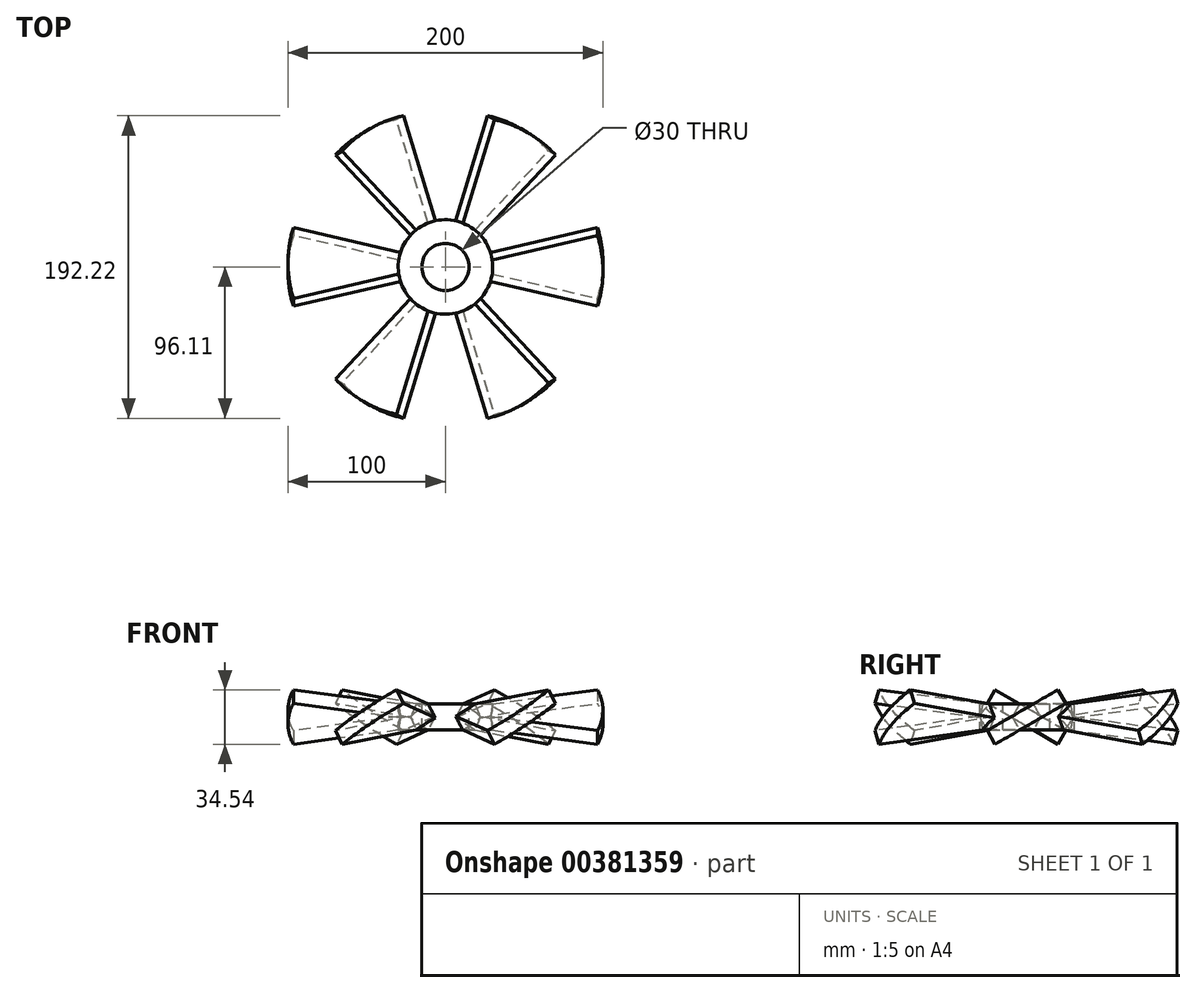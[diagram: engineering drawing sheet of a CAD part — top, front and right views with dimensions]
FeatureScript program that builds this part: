
annotation { "Feature Type Name" : "Feature", "Feature Type Description" : "" }
export const myFeature = defineFeature(function(context is Context, id is Id, definition is map)
    precondition{}
    {
        {
            var Q0;
            Q0=qCreatedBy(makeId("Top.planeOp"),FACE);
            var sketch = newSketch(context, id + "F0", { "sketchPlane" : qUnion([Q0])});
            skArc(sketch, "E0", {"start": v(96.6, 25.88) * mm, "mid": v(100, 0) * mm, "end": v(96.6, -25.88) * mm});
            skLineSegment(sketch, "E1", {"start": v(0, 0) * mm, "end": v(96.6, -25.88) * mm});
            skLineSegment(sketch, "E2.MirrorCS", {"start": v(0, 0) * mm, "end": v(96.6, 25.88) * mm});
            skLineSegment(sketch, "E3", {"start": v(0, 0) * mm, "end": v(116.16, 0) * mm, "construction": true});
            skSolve(sketch);
        }
        {
            var Q0;
            Q0 = qSketchRegion(id + "F0", true);
            extrude(context, id + "F1", {"entities" : qUnion([Q0]), "endBound" : BoundingType.SYMMETRIC, "depth" : 10 * mm});
        }
        {
            var Q0;
            Q0=makeQuery(id+"F1.opExtrude","SWEPT_BODY",BODY,{"disambiguationData":[OSD([sQuery(id+"F0.wireOp",EDGE,"E0"),sQuery(id+"F0.wireOp",EDGE,"E1"),sQuery(id+"F0.wireOp",EDGE,"E2.MirrorCS")])]});
            var Q1;
            Q1=sQuery(id+"F0.wireOp",EDGE,"E3");
            transform(context, id + "F2", {"entities" : qUnion([Q0]), "transformType" : TransformType.ROTATION, "transformAxis" : qUnion([Q1]), "angle" : 30 * degree, "makeCopy" : false});
        }
        {
            var Q0;
            Q0=qCreatedBy(makeId("Front.planeOp"),FACE);
            var sketch = newSketch(context, id + "F3", { "sketchPlane" : qUnion([Q0])});
            skLineSegment(sketch, "E4", {"start": v(0, 0) * mm, "end": v(0, 62.84) * mm, "construction": true});
            skSolve(sketch);
        }
        {
            var Q0;
            Q0=makeQuery(id+"F1.opExtrude","SWEPT_BODY",BODY,{"disambiguationData":[OSD([sQuery(id+"F0.wireOp",EDGE,"E0"),sQuery(id+"F0.wireOp",EDGE,"E1"),sQuery(id+"F0.wireOp",EDGE,"E2.MirrorCS")])]});
            var Q1;
            Q1=sQuery(id+"F3.wireOp",EDGE,"E4");
            circularPattern(context, id + "F4", {"entities" : qUnion([Q0]), "axis" : qUnion([Q1]), "angle" : 360 * degree, "instanceCount" : 6, "equalSpace" : true});
        }
        {
            var Q0;
            Q0=qCreatedBy(makeId("Top.planeOp"),FACE);
            var sketch = newSketch(context, id + "F5", { "sketchPlane" : qUnion([Q0])});
            skCircle(sketch, "E5", {"center": v(0, 0) * mm, "radius": 30 * mm});
            skSolve(sketch);
        }
        {
            var Q0;
            Q0 = qSketchRegion(id + "F5", true);
            extrude(context, id + "F6", {"entities" : qUnion([Q0]), "endBound" : BoundingType.SYMMETRIC, "depth" : 25 * mm});
        }
        {
            var Q0;
            Q0=makeQuery(id+"F6.opExtrude","SWEPT_BODY",BODY,{"disambiguationData":[OSD([sQuery(id+"F5.wireOp",EDGE,"E5")])]});
            var Q1;
            Q1=makeQuery(id+"F4.opPattern","COPY",BODY,{"derivedFrom":makeQuery(id+"F1.opExtrude","SWEPT_BODY",BODY,{"disambiguationData":[OSD([sQuery(id+"F0.wireOp",EDGE,"E0"),sQuery(id+"F0.wireOp",EDGE,"E1"),sQuery(id+"F0.wireOp",EDGE,"E2.MirrorCS")])]}),"instanceName":"4"});
            var Q2;
            Q2=makeQuery(id+"F4.opPattern","COPY",BODY,{"derivedFrom":makeQuery(id+"F1.opExtrude","SWEPT_BODY",BODY,{"disambiguationData":[OSD([sQuery(id+"F0.wireOp",EDGE,"E0"),sQuery(id+"F0.wireOp",EDGE,"E1"),sQuery(id+"F0.wireOp",EDGE,"E2.MirrorCS")])]}),"instanceName":"5"});
            var Q3;
            Q3=makeQuery(id+"F4.opPattern","COPY",BODY,{"derivedFrom":makeQuery(id+"F1.opExtrude","SWEPT_BODY",BODY,{"disambiguationData":[OSD([sQuery(id+"F0.wireOp",EDGE,"E0"),sQuery(id+"F0.wireOp",EDGE,"E1"),sQuery(id+"F0.wireOp",EDGE,"E2.MirrorCS")])]}),"instanceName":"3"});
            var Q4;
            Q4=makeQuery(id+"F4.opPattern","COPY",BODY,{"derivedFrom":makeQuery(id+"F1.opExtrude","SWEPT_BODY",BODY,{"disambiguationData":[OSD([sQuery(id+"F0.wireOp",EDGE,"E0"),sQuery(id+"F0.wireOp",EDGE,"E1"),sQuery(id+"F0.wireOp",EDGE,"E2.MirrorCS")])]}),"instanceName":"1"});
            var Q5;
            Q5=makeQuery(id+"F4.opPattern","COPY",BODY,{"derivedFrom":makeQuery(id+"F1.opExtrude","SWEPT_BODY",BODY,{"disambiguationData":[OSD([sQuery(id+"F0.wireOp",EDGE,"E0"),sQuery(id+"F0.wireOp",EDGE,"E1"),sQuery(id+"F0.wireOp",EDGE,"E2.MirrorCS")])]}),"instanceName":"2"});
            var Q6;
            Q6=makeQuery(id+"F1.opExtrude","SWEPT_BODY",BODY,{"disambiguationData":[OSD([sQuery(id+"F0.wireOp",EDGE,"E0"),sQuery(id+"F0.wireOp",EDGE,"E1"),sQuery(id+"F0.wireOp",EDGE,"E2.MirrorCS")])]});
            booleanBodies(context, id + "F7", {"operationType" : BooleanOperationType.UNION, "tools" : qUnion([Q0, Q1, Q2, Q3, Q4, Q5, Q6])});
        }
        {
            var Q0;
            {var subQ0=sQuery(id+"F0.wireOp",EDGE,"E2.MirrorCS");Q0=makeQuery(id+"F7.opBoolean","INTERSECT",VERTEX,{"derivedFrom":[makeQuery(id+"F4.opPattern","COPY",FACE,{"derivedFrom":makeQuery(id+"F1.opExtrude","CAP_FACE",FACE,{"disambiguationData":[OSD([sQuery(id+"F0.wireOp",EDGE,"E0"),sQuery(id+"F0.wireOp",EDGE,"E1"),subQ0])],"isStart":false}),"instanceName":"5"}),makeQuery(id+"F4.opPattern","COPY",FACE,{"derivedFrom":makeQuery(id+"F1.opExtrude","SWEPT_FACE",FACE,{"disambiguationData":[OSD([subQ0])]}),"instanceName":"5"}),makeQuery(id+"F6.opExtrude","SWEPT_FACE",FACE,{"disambiguationData":[OSD([sQuery(id+"F5.wireOp",EDGE,"E5")])]})]});}
            var Q1;
            {var subQ0=sQuery(id+"F0.wireOp",EDGE,"E2.MirrorCS");Q1=makeQuery(id+"F7.opBoolean","INTERSECT",VERTEX,{"derivedFrom":[makeQuery(id+"F4.opPattern","COPY",FACE,{"derivedFrom":makeQuery(id+"F1.opExtrude","CAP_FACE",FACE,{"disambiguationData":[OSD([sQuery(id+"F0.wireOp",EDGE,"E0"),sQuery(id+"F0.wireOp",EDGE,"E1"),subQ0])],"isStart":false}),"instanceName":"1"}),makeQuery(id+"F4.opPattern","COPY",FACE,{"derivedFrom":makeQuery(id+"F1.opExtrude","SWEPT_FACE",FACE,{"disambiguationData":[OSD([subQ0])]}),"instanceName":"1"}),makeQuery(id+"F6.opExtrude","SWEPT_FACE",FACE,{"disambiguationData":[OSD([sQuery(id+"F5.wireOp",EDGE,"E5")])]})]});}
            var Q2;
            {var subQ0=sQuery(id+"F0.wireOp",EDGE,"E2.MirrorCS");Q2=makeQuery(id+"F7.opBoolean","INTERSECT",VERTEX,{"derivedFrom":[makeQuery(id+"F4.opPattern","COPY",FACE,{"derivedFrom":makeQuery(id+"F1.opExtrude","CAP_FACE",FACE,{"disambiguationData":[OSD([sQuery(id+"F0.wireOp",EDGE,"E0"),sQuery(id+"F0.wireOp",EDGE,"E1"),subQ0])],"isStart":false}),"instanceName":"3"}),makeQuery(id+"F4.opPattern","COPY",FACE,{"derivedFrom":makeQuery(id+"F1.opExtrude","SWEPT_FACE",FACE,{"disambiguationData":[OSD([subQ0])]}),"instanceName":"3"}),makeQuery(id+"F6.opExtrude","SWEPT_FACE",FACE,{"disambiguationData":[OSD([sQuery(id+"F5.wireOp",EDGE,"E5")])]})]});}
            cPlane(context, id + "F8", {"entities" : qUnion([Q0, Q1, Q2]), "cplaneType" : CPlaneType.THREE_POINT, "offset" : 25 * mm, "width" : 150 * mm, "height" : 150 * mm});
        }
        {
            var Q0;
            Q0=makeQuery(id+"F6.opExtrude","CAP_FACE",FACE,{"disambiguationData":[OSD([sQuery(id+"F5.wireOp",EDGE,"E5")])],"isStart":false});
            var Q1;
            Q1=qCreatedBy(id+"F8.planeOp",FACE);
            extrude(context, id + "F9", {"entities" : qUnion([Q0]), "operationType" : NewBodyOperationType.REMOVE, "endBound" : BoundingType.UP_TO_SURFACE, "oppositeDirection" : true, "endBoundEntityFace" : qUnion([Q1]), "depth" : 25 * mm});
        }
        {
            var Q0;
            {var subQ0=sQuery(id+"F0.wireOp",EDGE,"E1");Q0=makeQuery(id+"F7.opBoolean","INTERSECT",VERTEX,{"derivedFrom":[makeQuery(id+"F1.opExtrude","CAP_FACE",FACE,{"disambiguationData":[OSD([sQuery(id+"F0.wireOp",EDGE,"E0"),subQ0,sQuery(id+"F0.wireOp",EDGE,"E2.MirrorCS")])],"isStart":true}),makeQuery(id+"F1.opExtrude","SWEPT_FACE",FACE,{"disambiguationData":[OSD([subQ0])]}),makeQuery(id+"F6.opExtrude","SWEPT_FACE",FACE,{"disambiguationData":[OSD([sQuery(id+"F5.wireOp",EDGE,"E5")])]})]});}
            var Q1;
            {var subQ0=sQuery(id+"F0.wireOp",EDGE,"E1");Q1=makeQuery(id+"F7.opBoolean","INTERSECT",VERTEX,{"derivedFrom":[makeQuery(id+"F4.opPattern","COPY",FACE,{"derivedFrom":makeQuery(id+"F1.opExtrude","CAP_FACE",FACE,{"disambiguationData":[OSD([sQuery(id+"F0.wireOp",EDGE,"E0"),subQ0,sQuery(id+"F0.wireOp",EDGE,"E2.MirrorCS")])],"isStart":true}),"instanceName":"4"}),makeQuery(id+"F4.opPattern","COPY",FACE,{"derivedFrom":makeQuery(id+"F1.opExtrude","SWEPT_FACE",FACE,{"disambiguationData":[OSD([subQ0])]}),"instanceName":"4"}),makeQuery(id+"F6.opExtrude","SWEPT_FACE",FACE,{"disambiguationData":[OSD([sQuery(id+"F5.wireOp",EDGE,"E5")])]})]});}
            var Q2;
            {var subQ0=sQuery(id+"F0.wireOp",EDGE,"E1");Q2=makeQuery(id+"F7.opBoolean","INTERSECT",VERTEX,{"derivedFrom":[makeQuery(id+"F4.opPattern","COPY",FACE,{"derivedFrom":makeQuery(id+"F1.opExtrude","CAP_FACE",FACE,{"disambiguationData":[OSD([sQuery(id+"F0.wireOp",EDGE,"E0"),subQ0,sQuery(id+"F0.wireOp",EDGE,"E2.MirrorCS")])],"isStart":true}),"instanceName":"2"}),makeQuery(id+"F4.opPattern","COPY",FACE,{"derivedFrom":makeQuery(id+"F1.opExtrude","SWEPT_FACE",FACE,{"disambiguationData":[OSD([subQ0])]}),"instanceName":"2"}),makeQuery(id+"F6.opExtrude","SWEPT_FACE",FACE,{"disambiguationData":[OSD([sQuery(id+"F5.wireOp",EDGE,"E5")])]})]});}
            cPlane(context, id + "F10", {"entities" : qUnion([Q0, Q1, Q2]), "cplaneType" : CPlaneType.THREE_POINT, "offset" : 25 * mm, "width" : 150 * mm, "height" : 150 * mm});
        }
        {
            var Q0;
            Q0=makeQuery(id+"F6.opExtrude","CAP_FACE",FACE,{"disambiguationData":[OSD([sQuery(id+"F5.wireOp",EDGE,"E5")])],"isStart":true});
            var Q1;
            Q1=qCreatedBy(id+"F10.planeOp",FACE);
            extrude(context, id + "F11", {"entities" : qUnion([Q0]), "operationType" : NewBodyOperationType.REMOVE, "endBound" : BoundingType.UP_TO_SURFACE, "oppositeDirection" : true, "endBoundEntityFace" : qUnion([Q1]), "depth" : 25 * mm});
        }
        {
            var Q0;
            Q0=makeQuery(id+"F9.boolean.opBoolean","COPY",FACE,{"derivedFrom":makeQuery(id+"F9.opExtrude","CAP_FACE",FACE,{"disambiguationData":[OSD([sQuery(id+"F5.wireOp",EDGE,"E5")])],"isStart":false})});
            var sketch = newSketch(context, id + "F12", { "sketchPlane" : qUnion([Q0])});
            skCircle(sketch, "E6", {"center": v(0, 0) * mm, "radius": 15 * mm});
            skSolve(sketch);
        }
        {
            var Q0;
            Q0=makeQuery(id+"F12.imprint","IMPRINT",FACE,{"disambiguationData":[TD([[makeQuery(id+"F12.imprint","IMPRINT",EDGE,{"derivedFrom":sQuery(id+"F12.wireOp",EDGE,"E6")}),1.0]])]});
            extrude(context, id + "F13", {"entities" : qUnion([Q0]), "operationType" : NewBodyOperationType.REMOVE, "endBound" : BoundingType.UP_TO_NEXT, "oppositeDirection" : true, "depth" : 25 * mm});
        }
    });
